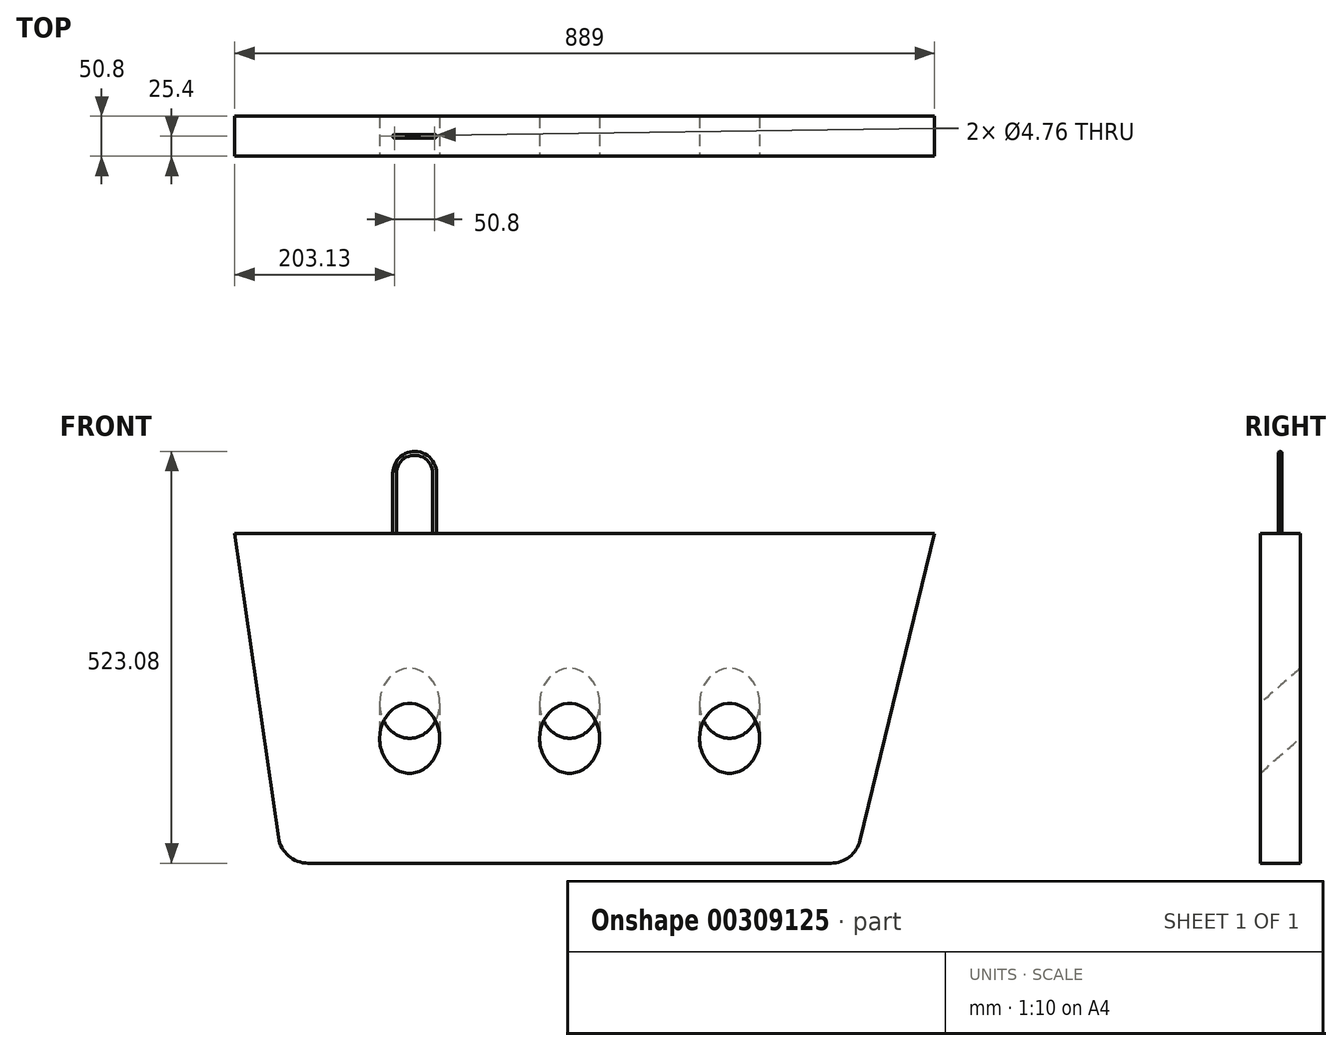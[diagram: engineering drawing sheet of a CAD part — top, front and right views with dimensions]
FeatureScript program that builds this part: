
annotation { "Feature Type Name" : "Feature", "Feature Type Description" : "" }
export const myFeature = defineFeature(function(context is Context, id is Id, definition is map)
    precondition{}
    {
        {
            var Q0;
            Q0=qCreatedBy(makeId("Front.planeOp"),FACE);
            var sketch = newSketch(context, id + "F0", { "sketchPlane" : qUnion([Q0])});
            skLineSegment(sketch, "E0", {"start": v(-369.76, 32.67) * mm, "end": v(-425.38, 419.1) * mm});
            skLineSegment(sketch, "E1", {"start": v(-425.38, 419.1) * mm, "end": v(463.62, 419.1) * mm});
            skLineSegment(sketch, "E2", {"start": v(463.62, 419.1) * mm, "end": v(369.08, 29.12) * mm});
            skLineSegment(sketch, "E3", {"start": v(332.05, 0) * mm, "end": v(-332.05, 0) * mm});
            skPoint(sketch, "E4.visualSharp", {"position": v(362.02, 0) * mm});
            skArc(sketch, "E4.filletArc", {"start": v(332.05, 0) * mm, "mid": v(355.6, 8.15) * mm, "end": v(369.08, 29.12) * mm});
            skLineSegment(sketch, "E5", {"start": v(332.05, 0) * mm, "end": v(362.02, 0) * mm, "construction": true});
            skLineSegment(sketch, "E6", {"start": v(369.08, 29.12) * mm, "end": v(362.02, 0) * mm, "construction": true});
            skPoint(sketch, "E7.visualSharp", {"position": v(-365.06, 0) * mm});
            skArc(sketch, "E7.filletArc", {"start": v(-369.76, 32.67) * mm, "mid": v(-357, 9.3) * mm, "end": v(-332.05, 0) * mm});
            skLineSegment(sketch, "E8", {"start": v(-369.76, 32.67) * mm, "end": v(-365.06, 0) * mm, "construction": true});
            skLineSegment(sketch, "E9", {"start": v(-365.06, 0) * mm, "end": v(-332.05, 0) * mm, "construction": true});
            skSolve(sketch);
        }
        {
            var Q0;
            Q0=makeQuery(id+"F0.imprint","IMPRINT",FACE,{"disambiguationData":[TD([[makeQuery(id+"F0.imprint","IMPRINT",EDGE,{"derivedFrom":sQuery(id+"F0.wireOp",EDGE,"E0")}),-1.0]])]});
            extrude(context, id + "F1", {"entities" : qUnion([Q0]), "depth" : 50.8 * mm});
        }
        {
            var Q0;
            Q0=makeQuery(id+"F1.opExtrude","CAP_FACE",FACE,{"disambiguationData":[OSD([sQuery(id+"F0.wireOp",EDGE,"E0"),sQuery(id+"F0.wireOp",EDGE,"E1"),sQuery(id+"F0.wireOp",EDGE,"E2"),sQuery(id+"F0.wireOp",EDGE,"E3"),sQuery(id+"F0.wireOp",EDGE,"E4.filletArc"),sQuery(id+"F0.wireOp",EDGE,"E7.filletArc")])],"isStart":false});
            var sketch = newSketch(context, id + "F2", { "sketchPlane" : qUnion([Q0])});
            skLineSegment(sketch, "E10.0", {"start": v(-369.76, 32.67) * mm, "end": v(-425.38, 419.1) * mm, "construction": true});
            skLineSegment(sketch, "E11.0", {"start": v(-425.38, 419.1) * mm, "end": v(463.62, 419.1) * mm, "construction": true});
            skLineSegment(sketch, "E12.0", {"start": v(463.62, 419.1) * mm, "end": v(369.08, 29.12) * mm, "construction": true});
            skArc(sketch, "E13.0", {"start": v(-369.76, 32.67) * mm, "mid": v(-357, 9.3) * mm, "end": v(-332.05, 0) * mm, "construction": true});
            skLineSegment(sketch, "E14.0", {"start": v(332.05, 0) * mm, "end": v(-332.05, 0) * mm, "construction": true});
            skArc(sketch, "E15.0", {"start": v(332.05, 0) * mm, "mid": v(355.6, 8.15) * mm, "end": v(369.08, 29.12) * mm, "construction": true});
            skPoint(sketch, "E16.0", {"position": v(0, 0) * mm});
            skEllipse(sketch, "E17", {"center": v(0, 158.75) * mm, "majorRadius": 44.45 * mm, "minorRadius": 38.1 * mm, "majorAxis": v(0, -1)});
            skEllipse(sketch, "E18.1.0.0", {"center": v(203.2, 158.75) * mm, "majorRadius": 44.45 * mm, "minorRadius": 38.1 * mm, "majorAxis": v(0, -1)});
            skLineSegment(sketch, "E18.direction1", {"start": v(0, 158.75) * mm, "end": v(203.2, 158.75) * mm, "construction": true});
            skEllipse(sketch, "E19.MirrorC", {"center": v(-203.2, 158.75) * mm, "majorRadius": 44.45 * mm, "minorRadius": 38.1 * mm, "majorAxis": v(0, -1)});
            skSolve(sketch);
        }
        {
            var Q0;
            Q0=qCreatedBy(makeId("Right.planeOp"),FACE);
            var sketch = newSketch(context, id + "F3", { "sketchPlane" : qUnion([Q0])});
            skLineSegment(sketch, "E20.0.0", {"start": v(0, 29.12) * mm, "end": v(0, 419.1) * mm});
            skLineSegment(sketch, "E20.0.1", {"start": v(0, 419.1) * mm, "end": v(-50.8, 419.1) * mm});
            skLineSegment(sketch, "E20.0.2", {"start": v(-50.8, 419.1) * mm, "end": v(-50.8, 29.12) * mm});
            skLineSegment(sketch, "E20.0.3", {"start": v(-50.8, 29.12) * mm, "end": v(0, 29.12) * mm});
            skPoint(sketch, "E21.0", {"position": v(-50.8, 158.75) * mm});
            skLineSegment(sketch, "E22", {"start": v(-50.8, 158.75) * mm, "end": v(0, 203.2) * mm});
            skSolve(sketch);
        }
        {
            var Q0;
            Q0=makeQuery(id+"F2.imprint","IMPRINT",FACE,{"disambiguationData":[TD([[makeQuery(id+"F2.imprint","IMPRINT",EDGE,{"derivedFrom":sQuery(id+"F2.wireOp",EDGE,"E19.MirrorC")}),1.0]])]});
            var Q1;
            Q1=makeQuery(id+"F2.imprint","IMPRINT",FACE,{"disambiguationData":[TD([[makeQuery(id+"F2.imprint","IMPRINT",EDGE,{"derivedFrom":sQuery(id+"F2.wireOp",EDGE,"E17")}),1.0]])]});
            var Q2;
            Q2=makeQuery(id+"F2.imprint","IMPRINT",FACE,{"disambiguationData":[TD([[makeQuery(id+"F2.imprint","IMPRINT",EDGE,{"derivedFrom":sQuery(id+"F2.wireOp",EDGE,"E18.1.0.0")}),1.0]])]});
            var Q3;
            Q3=sQuery(id+"F3.wireOp",EDGE,"E22");
            sweep(context, id + "F4", {"operationType" : NewBodyOperationType.REMOVE, "profiles" : qUnion([Q0, Q1, Q2]), "path" : qUnion([Q3])});
        }
        {
            var Q0;
            Q0=makeQuery(id+"F1.opExtrude","SWEPT_FACE",FACE,{"disambiguationData":[OSD([sQuery(id+"F0.wireOp",EDGE,"E1")])]});
            var sketch = newSketch(context, id + "F5", { "sketchPlane" : qUnion([Q0])});
            skCircle(sketch, "E23", {"center": v(-222.25, -25.4) * mm, "radius": 2.38 * mm});
            skSolve(sketch);
        }
        {
            var Q0;
            Q0=qCreatedBy(makeId("Front.planeOp"),FACE);
            var sketch = newSketch(context, id + "F6", { "sketchPlane" : qUnion([Q0])});
            skPoint(sketch, "E24.0", {"position": v(-222.25, 419.1) * mm});
            skLineSegment(sketch, "E25", {"start": v(-222.25, 419.1) * mm, "end": v(-222.25, 495.3) * mm});
            skLineSegment(sketch, "E26", {"start": v(-222.25, 495.3) * mm, "end": v(-171.45, 495.3) * mm, "construction": true});
            skLineSegment(sketch, "E27", {"start": v(-171.45, 495.3) * mm, "end": v(-171.45, 419.1) * mm});
            skArc(sketch, "E28", {"start": v(-171.45, 495.3) * mm, "mid": v(-196.85, 520.7) * mm, "end": v(-222.25, 495.3) * mm});
            skLineSegment(sketch, "E29", {"start": v(-222.25, 419.1) * mm, "end": v(-171.45, 419.1) * mm, "construction": true});
            skSolve(sketch);
        }
        {
            var Q0;
            Q0=makeQuery(id+"F5.imprint","IMPRINT",FACE,{"disambiguationData":[TD([[makeQuery(id+"F5.imprint","IMPRINT",EDGE,{"derivedFrom":sQuery(id+"F5.wireOp",EDGE,"E23")}),1.0]])]});
            var Q1;
            Q1=sQuery(id+"F6.wireOp",EDGE,"E25");
            var Q2;
            Q2=sQuery(id+"F6.wireOp",EDGE,"E28");
            var Q3;
            Q3=sQuery(id+"F6.wireOp",EDGE,"E27");
            sweep(context, id + "F7", {"operationType" : NewBodyOperationType.ADD, "profiles" : qUnion([Q0]), "path" : qUnion([Q1, Q2, Q3])});
        }
        {
            var Q0;
            Q0=makeQuery(id+"F1.opExtrude","SWEPT_FACE",FACE,{"disambiguationData":[OSD([sQuery(id+"F0.wireOp",EDGE,"E1")])]});
            var sketch = newSketch(context, id + "F8", { "sketchPlane" : qUnion([Q0])});
            skLineSegment(sketch, "E30.0.0", {"start": v(463.62, 0) * mm, "end": v(-425.38, 0) * mm});
            skLineSegment(sketch, "E30.0.1", {"start": v(-425.38, 0) * mm, "end": v(-425.38, -50.8) * mm});
            skLineSegment(sketch, "E30.0.2", {"start": v(-425.38, -50.8) * mm, "end": v(463.62, -50.8) * mm});
            skLineSegment(sketch, "E30.0.3", {"start": v(463.62, -50.8) * mm, "end": v(463.62, 0) * mm});
            skSolve(sketch);
        }
        {
            var Q0;
            Q0=makeQuery(id+"F8.imprint","IMPRINT",FACE,{"disambiguationData":[TD([[makeQuery(id+"F8.imprint","IMPRINT",EDGE,{"derivedFrom":sQuery(id+"F8.wireOp",EDGE,"E30.0.0")}),-1.0]])]});
            extrude(context, id + "F9", {"entities" : qUnion([Q0]), "depth" : 0 * mm});
        }
    });
